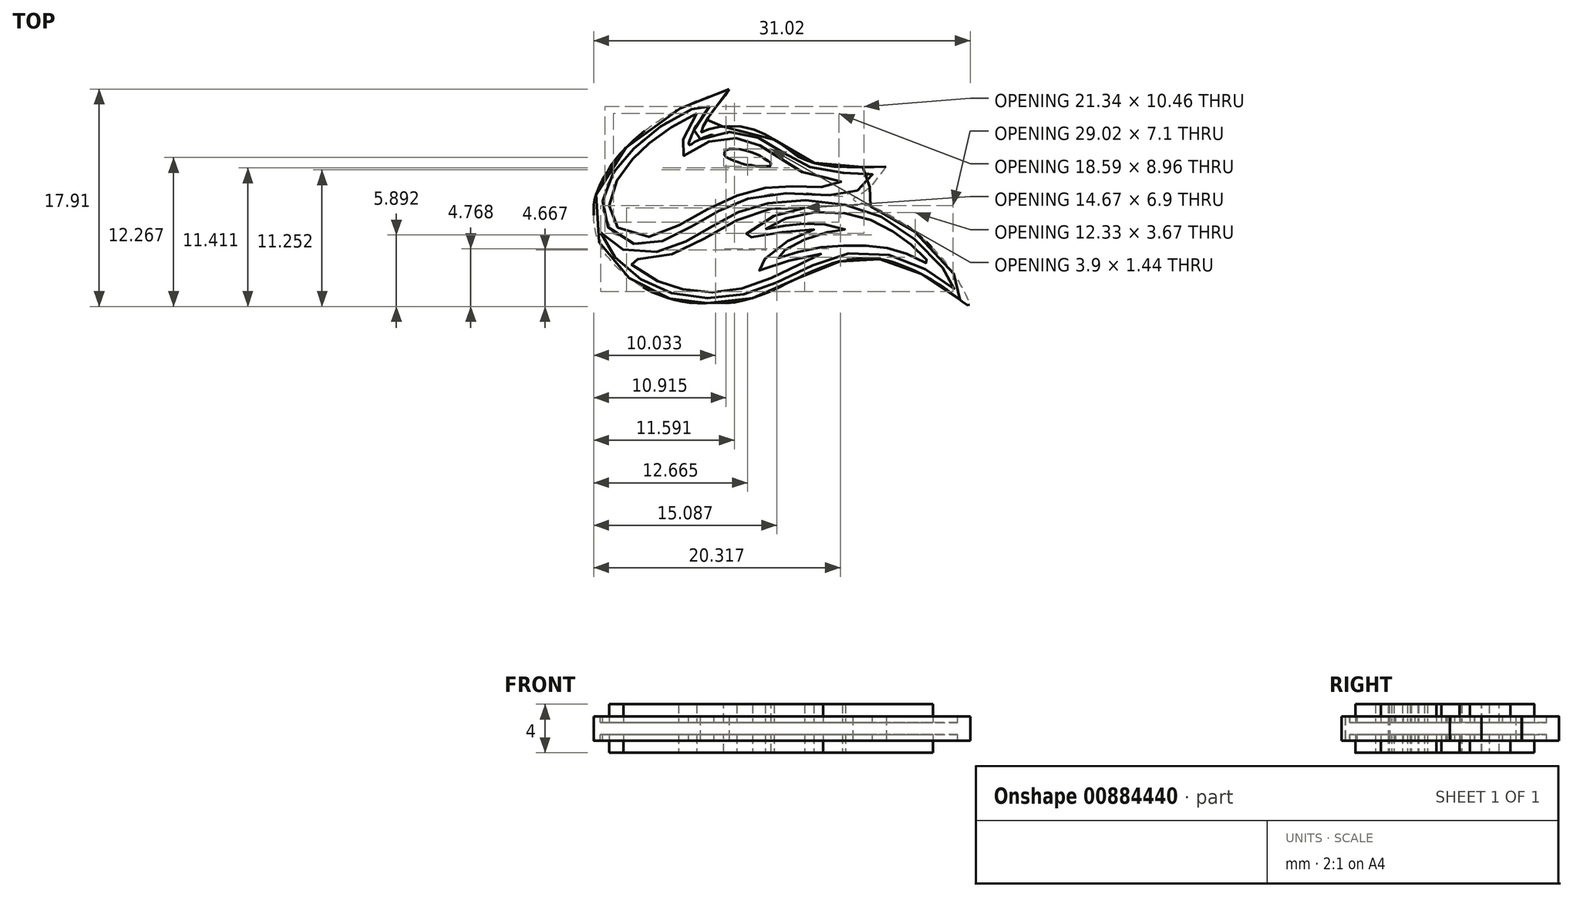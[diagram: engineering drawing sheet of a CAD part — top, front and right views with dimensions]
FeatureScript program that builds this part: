
annotation { "Feature Type Name" : "Feature", "Feature Type Description" : "" }
export const myFeature = defineFeature(function(context is Context, id is Id, definition is map)
    precondition{}
    {
        {
            var Q0;
            Q0=qCreatedBy(makeId("Top.planeOp"),FACE);
            var sketch = newSketch(context, id + "F0", { "sketchPlane" : qUnion([Q0])});
            skFitSpline(sketch, "E0", {"points": [v(-3.9, 9.38) * mm, v(-3.91, 9.32) * mm, v(-3.98, 9.21) * mm, v(-4.07, 9.09) * mm, v(-4.2, 8.93) * mm, v(-4.32, 8.78) * mm, v(-4.45, 8.61) * mm, v(-4.55, 8.47) * mm, v(-4.7, 8.28) * mm, v(-4.84, 8.11) * mm, v(-4.97, 7.93) * mm, v(-5.14, 7.74) * mm, v(-5.25, 7.58) * mm, v(-5.4, 7.4) * mm, v(-5.51, 7.23) * mm, v(-5.62, 7.08) * mm, v(-5.78, 6.83) * mm, v(-5.93, 6.6) * mm, v(-6, 6.44) * mm, v(-6.07, 6.28) * mm, v(-6.16, 6.11) * mm, v(-6.27, 5.97) * mm, v(-6.27, 5.87) * mm, v(-6.19, 5.85) * mm, v(-6.07, 5.91) * mm, v(-5.96, 5.94) * mm, v(-5.82, 6) * mm, v(-5.68, 6.05) * mm, v(-5.4, 6.13) * mm, v(-5.14, 6.2) * mm, v(-4.9, 6.26) * mm, v(-4.67, 6.3) * mm, v(-4.42, 6.32) * mm, v(-4.1, 6.34) * mm, v(-3.84, 6.34) * mm, v(-3.55, 6.33) * mm, v(-3.13, 6.33) * mm, v(-2.75, 6.3) * mm, v(-2.21, 6.16) * mm, v(-1.86, 6.04) * mm, v(-1.54, 5.92) * mm, v(-1.2, 5.78) * mm, v(-0.87, 5.63) * mm, v(-0.3, 5.3) * mm, v(0.1, 5.07) * mm, v(0.39, 4.86) * mm, v(0.8, 4.57) * mm, v(1.1, 4.33) * mm, v(1.5, 4.04) * mm, v(1.65, 3.9) * mm, v(1.9, 3.77) * mm, v(2, 3.7) * mm, v(2.22, 3.61) * mm, v(2.51, 3.51) * mm, v(2.63, 3.45) * mm, v(2.81, 3.42) * mm, v(3, 3.34) * mm, v(3.19, 3.28) * mm, v(3.49, 3.23) * mm, v(3.66, 3.16) * mm, v(3.9, 3.14) * mm, v(4.15, 3.12) * mm, v(4.42, 3.1) * mm, v(4.58, 3.04) * mm, v(4.9, 3) * mm, v(5.21, 3) * mm, v(5.71, 2.98) * mm, v(6.19, 2.98) * mm, v(6.67, 2.97) * mm, v(7.27, 2.98) * mm, v(7.68, 2.98) * mm, v(8.02, 2.98) * mm, v(8.43, 2.98) * mm, v(8.85, 3) * mm, v(9.02, 3) * mm, v(8.98, 2.92) * mm, v(8.74, 2.64) * mm, v(8.59, 2.42) * mm, v(8.3, 2.07) * mm, v(8.12, 1.82) * mm, v(7.95, 1.61) * mm, v(7.72, 1.36) * mm, v(7.51, 1.17) * mm, v(7.23, 0.94) * mm, v(7, 0.77) * mm, v(6.85, 0.64) * mm, v(6.63, 0.49) * mm, v(6.49, 0.42) * mm, v(6.37, 0.42) * mm, v(6.3, 0.38) * mm, v(6.29, 0.3) * mm, v(6.35, 0.25) * mm, v(6.47, 0.16) * mm, v(6.67, 0.12) * mm, v(6.88, 0.07) * mm, v(7.23, -0.05) * mm, v(7.57, -0.2) * mm, v(7.95, -0.34) * mm, v(8.36, -0.48) * mm, v(8.59, -0.6) * mm, v(8.98, -0.8) * mm, v(9.31, -0.98) * mm, v(9.63, -1.16) * mm, v(9.92, -1.34) * mm, v(10.16, -1.49) * mm, v(10.47, -1.68) * mm, v(10.78, -1.9) * mm, v(11.14, -2.17) * mm, v(11.43, -2.39) * mm, v(11.73, -2.62) * mm, v(12.02, -2.9) * mm, v(12.3, -3.12) * mm, v(12.66, -3.5) * mm, v(13, -3.84) * mm, v(13.23, -4.13) * mm, v(13.6, -4.5) * mm, v(13.87, -4.85) * mm, v(14.2, -5.31) * mm, v(14.55, -5.74) * mm, v(14.77, -6.1) * mm, v(15.02, -6.5) * mm, v(15.21, -6.85) * mm, v(15.4, -7.2) * mm, v(15.55, -7.47) * mm, v(15.7, -7.8) * mm, v(15.86, -8.15) * mm, v(15.92, -8.36) * mm, v(15.95, -8.5) * mm, v(15.74, -8.42) * mm, v(15.5, -8.22) * mm, v(15.25, -8.05) * mm, v(14.97, -7.83) * mm, v(14.64, -7.6) * mm, v(14.34, -7.38) * mm, v(14.17, -7.23) * mm, v(13.97, -7.09) * mm, v(13.68, -6.89) * mm, v(13.42, -6.72) * mm, v(13.16, -6.55) * mm, v(12.96, -6.42) * mm, v(12.72, -6.26) * mm, v(12.38, -6.07) * mm, v(12.15, -5.95) * mm, v(11.95, -5.85) * mm, v(11.7, -5.72) * mm, v(11.47, -5.6) * mm, v(11.22, -5.47) * mm, v(10.97, -5.37) * mm, v(10.74, -5.28) * mm, v(10.46, -5.18) * mm, v(10.16, -5.06) * mm, v(9.87, -4.94) * mm, v(9.64, -4.87) * mm, v(9.43, -4.79) * mm, v(9.16, -4.72) * mm, v(8.89, -4.65) * mm, v(8.63, -4.61) * mm, v(8.44, -4.6) * mm, v(8.2, -4.57) * mm, v(7.93, -4.54) * mm, v(7.58, -4.53) * mm, v(7.3, -4.54) * mm, v(7, -4.54) * mm, v(6.68, -4.54) * mm, v(6.49, -4.54) * mm, v(6.31, -4.58) * mm, v(6.15, -4.63) * mm, v(5.98, -4.66) * mm, v(5.74, -4.66) * mm, v(5.6, -4.69) * mm, v(5.44, -4.74) * mm, v(5.25, -4.77) * mm, v(5.09, -4.81) * mm, v(4.93, -4.86) * mm, v(4.83, -4.9) * mm, v(4.53, -4.97) * mm, v(4.2, -5.11) * mm, v(3.79, -5.26) * mm, v(3.54, -5.36) * mm, v(3.19, -5.5) * mm, v(2.96, -5.6) * mm, v(2.62, -5.77) * mm, v(2.36, -5.87) * mm, v(2.1, -6) * mm, v(1.88, -6.1) * mm, v(1.6, -6.24) * mm, v(1.36, -6.38) * mm, v(0.95, -6.56) * mm, v(0.58, -6.75) * mm, v(0.27, -6.9) * mm, v(-0.17, -7.08) * mm, v(-0.45, -7.23) * mm, v(-0.7, -7.35) * mm, v(-1.06, -7.49) * mm, v(-1.36, -7.59) * mm, v(-1.55, -7.66) * mm, v(-1.75, -7.74) * mm, v(-2.02, -7.82) * mm, v(-2.28, -7.9) * mm, v(-2.53, -7.97) * mm, v(-2.86, -8.05) * mm, v(-3.1, -8.13) * mm, v(-3.3, -8.16) * mm, v(-3.58, -8.2) * mm, v(-3.83, -8.21) * mm, v(-4.07, -8.22) * mm, v(-4.38, -8.22) * mm, v(-4.72, -8.2) * mm, v(-5.09, -8.2) * mm, v(-5.41, -8.2) * mm, v(-5.72, -8.22) * mm, v(-6.05, -8.21) * mm, v(-6.28, -8.23) * mm, v(-6.53, -8.22) * mm, v(-6.79, -8.23) * mm, v(-7, -8.21) * mm, v(-7.19, -8.2) * mm, v(-7.37, -8.16) * mm, v(-7.52, -8.15) * mm, v(-7.69, -8.11) * mm, v(-7.88, -8.1) * mm, v(-8.05, -8.06) * mm, v(-8.26, -8.02) * mm, v(-8.45, -7.96) * mm, v(-8.6, -7.91) * mm, v(-8.74, -7.88) * mm, v(-8.93, -7.81) * mm, v(-9.1, -7.76) * mm, v(-9.31, -7.7) * mm, v(-9.53, -7.6) * mm, v(-9.68, -7.55) * mm, v(-10.04, -7.42) * mm, v(-10.3, -7.3) * mm, v(-10.52, -7.19) * mm, v(-10.95, -6.96) * mm, v(-11.26, -6.77) * mm, v(-11.52, -6.6) * mm, v(-11.81, -6.4) * mm, v(-12.06, -6.23) * mm, v(-12.23, -6.08) * mm, v(-12.43, -5.93) * mm, v(-12.68, -5.72) * mm, v(-12.9, -5.53) * mm, v(-13.11, -5.32) * mm, v(-13.37, -5.05) * mm, v(-13.6, -4.76) * mm, v(-13.83, -4.5) * mm, v(-14.07, -4.23) * mm, v(-14.21, -3.97) * mm, v(-14.37, -3.74) * mm, v(-14.47, -3.5) * mm, v(-14.61, -3.23) * mm, v(-14.7, -3) * mm, v(-14.8, -2.77) * mm, v(-14.86, -2.53) * mm, v(-14.94, -2.3) * mm, v(-15, -1.83) * mm, v(-15.05, -1.58) * mm, v(-15.06, -1.24) * mm, v(-15.06, -0.85) * mm, v(-15.06, -0.53) * mm, v(-15.06, -0.3) * mm, v(-15, 0.2) * mm, v(-14.9, 0.6) * mm, v(-14.74, 1.08) * mm, v(-14.58, 1.42) * mm, v(-14.4, 1.83) * mm, v(-14.22, 2.15) * mm, v(-14.06, 2.42) * mm, v(-13.87, 2.7) * mm, v(-13.7, 3) * mm, v(-13.48, 3.3) * mm, v(-13.33, 3.51) * mm, v(-12.9, 4.05) * mm, v(-12.45, 4.52) * mm, v(-12.12, 4.83) * mm, v(-11.55, 5.38) * mm, v(-10.67, 6.1) * mm, v(-10.27, 6.4) * mm, v(-9.8, 6.73) * mm, v(-9.18, 7.11) * mm, v(-8.74, 7.38) * mm, v(-8.38, 7.58) * mm, v(-7.98, 7.79) * mm, v(-7.6, 8) * mm, v(-7.21, 8.15) * mm, v(-6.78, 8.36) * mm, v(-6.4, 8.5) * mm, v(-5.87, 8.72) * mm, v(-5.4, 8.9) * mm, v(-4.9, 9.08) * mm, v(-4.53, 9.2) * mm, v(-4.26, 9.3) * mm, v(-4.07, 9.37) * mm, v(-3.99, 9.4) * mm, v(-3.9, 9.38) * mm]});
            skFitSpline(sketch, "E1", {"points": [v(-5.52, 7.97) * mm, v(-5.3, 8.2) * mm, v(-5.17, 8.38) * mm, v(-5.51, 8.31) * mm, v(-5.76, 8.21) * mm, v(-6.27, 8.02) * mm, v(-6.63, 7.88) * mm, v(-6.9, 7.78) * mm, v(-7.32, 7.59) * mm, v(-7.78, 7.35) * mm, v(-8.2, 7.15) * mm, v(-8.66, 6.87) * mm, v(-9.12, 6.61) * mm, v(-9.46, 6.4) * mm, v(-9.72, 6.19) * mm, v(-10.04, 5.98) * mm, v(-10.31, 5.76) * mm, v(-10.75, 5.43) * mm, v(-11.11, 5.1) * mm, v(-11.47, 4.8) * mm, v(-11.86, 4.43) * mm, v(-12.13, 4.17) * mm, v(-12.41, 3.83) * mm, v(-12.7, 3.51) * mm, v(-12.94, 3.24) * mm, v(-13.17, 2.9) * mm, v(-13.4, 2.6) * mm, v(-13.45, 2.5) * mm, v(-13.63, 2.18) * mm, v(-13.8, 1.81) * mm, v(-14.02, 1.4) * mm, v(-14.1, 1.1) * mm, v(-14.24, 0.8) * mm, v(-14.28, 0.39) * mm, v(-14.34, 0.2) * mm, v(-14.32, 0) * mm, v(-14.34, -0.25) * mm, v(-14.32, -0.65) * mm, v(-14.3, -0.9) * mm, v(-14.24, -1.15) * mm, v(-14.16, -1.4) * mm, v(-14.03, -1.74) * mm, v(-13.87, -2) * mm, v(-13.63, -2.28) * mm, v(-13.43, -2.52) * mm, v(-13.05, -2.83) * mm, v(-12.58, -3.08) * mm, v(-12.27, -3.21) * mm, v(-12.03, -3.31) * mm, v(-11.75, -3.36) * mm, v(-11.5, -3.38) * mm, v(-11.25, -3.4) * mm, v(-10.9, -3.4) * mm, v(-10.57, -3.38) * mm, v(-10.28, -3.34) * mm, v(-9.92, -3.25) * mm, v(-9.55, -3.17) * mm, v(-9.32, -3.07) * mm, v(-9.07, -2.98) * mm, v(-8.78, -2.87) * mm, v(-8.43, -2.68) * mm, v(-8.08, -2.51) * mm, v(-7.62, -2.26) * mm, v(-7.08, -1.96) * mm, v(-6.73, -1.75) * mm, v(-6.35, -1.52) * mm, v(-6.07, -1.38) * mm, v(-5.75, -1.2) * mm, v(-5.4, -0.98) * mm, v(-5.1, -0.81) * mm, v(-4.84, -0.67) * mm, v(-4.49, -0.54) * mm, v(-4.18, -0.36) * mm, v(-3.9, -0.21) * mm, v(-3.57, -0.06) * mm, v(-3.17, 0.12) * mm, v(-2.79, 0.25) * mm, v(-2.4, 0.36) * mm, v(-1.86, 0.5) * mm, v(-1.32, 0.64) * mm, v(-0.8, 0.74) * mm, v(-0.26, 0.8) * mm, v(0.32, 0.83) * mm, v(1.01, 0.82) * mm, v(1.76, 0.84) * mm, v(2.44, 0.85) * mm, v(3.25, 0.82) * mm, v(3.97, 0.72) * mm, v(4.46, 0.63) * mm, v(4.92, 0.55) * mm, v(5.37, 0.55) * mm, v(5.74, 0.61) * mm, v(5.96, 0.7) * mm, v(6.28, 0.83) * mm, v(6.44, 0.91) * mm, v(6.6, 1.02) * mm, v(6.75, 1.13) * mm, v(6.91, 1.26) * mm, v(7.07, 1.38) * mm, v(7.23, 1.55) * mm, v(7.45, 1.76) * mm, v(7.58, 1.9) * mm, v(7.7, 2.05) * mm, v(7.79, 2.15) * mm, v(7.89, 2.26) * mm, v(7.9, 2.36) * mm, v(7.78, 2.47) * mm, v(7.63, 2.47) * mm, v(7.4, 2.47) * mm, v(7.1, 2.47) * mm, v(6.83, 2.46) * mm, v(6.4, 2.45) * mm, v(5.85, 2.48) * mm, v(5.38, 2.5) * mm, v(4.98, 2.53) * mm, v(4.49, 2.57) * mm, v(4.15, 2.65) * mm, v(3.64, 2.74) * mm, v(3.22, 2.82) * mm, v(2.83, 2.94) * mm, v(2.5, 3.04) * mm, v(2.2, 3.15) * mm, v(1.9, 3.27) * mm, v(1.55, 3.44) * mm, v(1.13, 3.74) * mm, v(0.89, 3.92) * mm, v(0.62, 4.1) * mm, v(0.4, 4.31) * mm, v(0.16, 4.46) * mm, v(-0.12, 4.64) * mm, v(-0.45, 4.84) * mm, v(-0.81, 5.04) * mm, v(-1.17, 5.25) * mm, v(-1.36, 5.33) * mm, v(-1.51, 5.4) * mm, v(-1.84, 5.52) * mm, v(-2.09, 5.62) * mm, v(-2.4, 5.7) * mm, v(-2.8, 5.76) * mm, v(-3.26, 5.79) * mm, v(-3.53, 5.85) * mm, v(-3.8, 5.87) * mm, v(-4.07, 5.87) * mm, v(-4.45, 5.84) * mm, v(-4.88, 5.76) * mm, v(-5.24, 5.66) * mm, v(-5.34, 5.63) * mm, v(-5.64, 5.53) * mm, v(-6.02, 5.39) * mm, v(-6.4, 5.23) * mm, v(-6.77, 5.04) * mm, v(-7.05, 4.83) * mm, v(-7.22, 4.79) * mm, v(-7.2, 5.08) * mm, v(-7.1, 5.36) * mm, v(-7, 5.59) * mm, v(-6.86, 5.93) * mm, v(-6.68, 6.27) * mm, v(-6.47, 6.6) * mm, v(-6.24, 6.9) * mm, v(-6.1, 7.16) * mm, v(-5.94, 7.42) * mm, v(-5.8, 7.59) * mm, v(-5.65, 7.75) * mm, v(-5.52, 7.97) * mm]});
            skFitSpline(sketch, "E2", {"points": [v(-14.5, -2.43) * mm, v(-14.32, -2.6) * mm, v(-14.14, -2.81) * mm, v(-13.88, -3.03) * mm, v(-13.76, -3.2) * mm, v(-13.49, -3.34) * mm, v(-13.28, -3.52) * mm, v(-12.98, -3.72) * mm, v(-12.65, -3.82) * mm, v(-12.34, -3.92) * mm, v(-12.05, -4.02) * mm, v(-11.75, -4.1) * mm, v(-11.17, -4.15) * mm, v(-10.73, -4.1) * mm, v(-10.16, -4.04) * mm, v(-9.74, -3.99) * mm, v(-9.4, -3.91) * mm, v(-9, -3.78) * mm, v(-8.67, -3.68) * mm, v(-8.36, -3.55) * mm, v(-8, -3.4) * mm, v(-7.71, -3.27) * mm, v(-7.42, -3.12) * mm, v(-6.99, -2.89) * mm, v(-6.7, -2.73) * mm, v(-6.34, -2.55) * mm, v(-6.16, -2.43) * mm, v(-5.94, -2.32) * mm, v(-5.7, -2.16) * mm, v(-5.45, -2.02) * mm, v(-5.13, -1.81) * mm, v(-4.84, -1.65) * mm, v(-4.54, -1.44) * mm, v(-4.25, -1.31) * mm, v(-3.95, -1.13) * mm, v(-3.72, -1.04) * mm, v(-3.47, -0.87) * mm, v(-3.15, -0.73) * mm, v(-2.88, -0.62) * mm, v(-2.57, -0.5) * mm, v(-2.24, -0.4) * mm, v(-1.92, -0.27) * mm, v(-1.57, -0.21) * mm, v(-1.4, -0.19) * mm, v(-1.06, -0.08) * mm, v(-0.34, 0.08) * mm, v(0, 0.1) * mm, v(0.2, 0.1) * mm, v(0.62, 0.14) * mm, v(1.2, 0.2) * mm, v(1.66, 0.22) * mm, v(2.52, 0.23) * mm, v(3.02, 0.17) * mm, v(3.45, 0.15) * mm, v(3.75, 0.12) * mm, v(4.3, 0.1) * mm, v(5.28, -0.08) * mm, v(5.8, -0.17) * mm, v(6.36, -0.29) * mm, v(6.83, -0.46) * mm, v(7.34, -0.62) * mm, v(7.87, -0.8) * mm, v(8.33, -1) * mm, v(8.87, -1.26) * mm, v(9.4, -1.58) * mm, v(9.89, -1.84) * mm, v(10.47, -2.25) * mm, v(10.87, -2.53) * mm, v(11.29, -2.89) * mm, v(11.75, -3.3) * mm, v(12.2, -3.67) * mm, v(12.56, -4.08) * mm, v(12.96, -4.52) * mm, v(13.4, -5.02) * mm, v(13.7, -5.34) * mm, v(13.9, -5.65) * mm, v(14.2, -6.08) * mm, v(14.52, -6.46) * mm, v(14.7, -6.74) * mm, v(14.85, -7.03) * mm, v(14.92, -7.21) * mm, v(14.66, -7.06) * mm, v(14.36, -6.81) * mm, v(14.1, -6.6) * mm, v(13.7, -6.32) * mm, v(13.37, -6.14) * mm, v(13.03, -5.9) * mm, v(12.49, -5.57) * mm, v(12.03, -5.32) * mm, v(11.46, -5.03) * mm, v(11.02, -4.84) * mm, v(10.64, -4.67) * mm, v(10.15, -4.51) * mm, v(9.58, -4.34) * mm, v(8.82, -4.17) * mm, v(8.22, -4.06) * mm, v(7.51, -4.03) * mm, v(6.8, -4.05) * mm, v(6.4, -4.07) * mm, v(5.89, -4.15) * mm, v(5.4, -4.27) * mm, v(4.92, -4.38) * mm, v(4.3, -4.58) * mm, v(3.84, -4.76) * mm, v(3.38, -4.95) * mm, v(2.93, -5.15) * mm, v(2.15, -5.54) * mm, v(1.58, -5.79) * mm, v(1.05, -6.04) * mm, v(0.63, -6.25) * mm, v(0.18, -6.44) * mm, v(-0.19, -6.61) * mm, v(-0.57, -6.77) * mm, v(-1.02, -6.93) * mm, v(-1.49, -7.13) * mm, v(-1.87, -7.25) * mm, v(-2.27, -7.36) * mm, v(-2.68, -7.5) * mm, v(-2.99, -7.56) * mm, v(-3.49, -7.67) * mm, v(-3.84, -7.78) * mm, v(-4.42, -7.8) * mm, v(-4.79, -7.83) * mm, v(-5.45, -7.82) * mm, v(-6, -7.82) * mm, v(-6.49, -7.81) * mm, v(-6.99, -7.74) * mm, v(-7.38, -7.68) * mm, v(-7.91, -7.6) * mm, v(-8.36, -7.5) * mm, v(-8.83, -7.35) * mm, v(-9.22, -7.21) * mm, v(-9.62, -7.04) * mm, v(-10, -6.92) * mm, v(-10.28, -6.78) * mm, v(-10.66, -6.58) * mm, v(-11.08, -6.35) * mm, v(-11.4, -6.12) * mm, v(-11.7, -5.93) * mm, v(-12.04, -5.7) * mm, v(-12.34, -5.42) * mm, v(-12.63, -5.16) * mm, v(-12.93, -4.87) * mm, v(-13.32, -4.45) * mm, v(-13.48, -4.23) * mm, v(-13.7, -3.9) * mm, v(-13.93, -3.57) * mm, v(-14.14, -3.26) * mm, v(-14.32, -2.99) * mm, v(-14.43, -2.77) * mm, v(-14.5, -2.57) * mm, v(-14.5, -2.43) * mm]});
            skFitSpline(sketch, "E3", {"points": [v(-6.57, 7.38) * mm, v(-6.74, 7.11) * mm, v(-6.9, 6.93) * mm, v(-7.03, 6.75) * mm, v(-7.13, 6.6) * mm, v(-7.22, 6.41) * mm, v(-7.3, 6.22) * mm, v(-7.38, 6.01) * mm, v(-7.47, 5.8) * mm, v(-7.59, 5.55) * mm, v(-7.66, 5.3) * mm, v(-7.75, 5.06) * mm, v(-7.8, 4.86) * mm, v(-7.85, 4.61) * mm, v(-7.92, 4.4) * mm, v(-7.97, 4.2) * mm, v(-8.02, 4.03) * mm, v(-8.04, 3.88) * mm, v(-8.07, 3.71) * mm, v(-8.03, 3.66) * mm, v(-7.9, 3.69) * mm, v(-7.82, 3.77) * mm, v(-7.65, 3.9) * mm, v(-7.47, 4.02) * mm, v(-7.27, 4.15) * mm, v(-7.13, 4.25) * mm, v(-6.98, 4.33) * mm, v(-6.8, 4.42) * mm, v(-6.61, 4.53) * mm, v(-6.44, 4.63) * mm, v(-6.22, 4.76) * mm, v(-5.92, 4.9) * mm, v(-5.67, 5.04) * mm, v(-5.42, 5.1) * mm, v(-5.18, 5.16) * mm, v(-4.96, 5.22) * mm, v(-4.74, 5.28) * mm, v(-4.52, 5.32) * mm, v(-4.3, 5.36) * mm, v(-4.14, 5.4) * mm, v(-3.97, 5.41) * mm, v(-3.78, 5.4) * mm, v(-3.57, 5.4) * mm, v(-3.35, 5.36) * mm, v(-3.14, 5.34) * mm, v(-3.01, 5.31) * mm, v(-2.84, 5.27) * mm, v(-2.66, 5.23) * mm, v(-2.45, 5.2) * mm, v(-2.3, 5.14) * mm, v(-2.13, 5.08) * mm, v(-1.97, 5.03) * mm, v(-1.81, 4.98) * mm, v(-1.67, 4.91) * mm, v(-1.54, 4.85) * mm, v(-1.38, 4.76) * mm, v(-1.18, 4.66) * mm, v(-0.98, 4.58) * mm, v(-0.85, 4.5) * mm, v(-0.69, 4.4) * mm, v(-0.55, 4.32) * mm, v(-0.4, 4.23) * mm, v(-0.22, 4.1) * mm, v(-0.08, 3.99) * mm, v(0.12, 3.85) * mm, v(0.24, 3.74) * mm, v(0.37, 3.65) * mm, v(0.51, 3.55) * mm, v(0.62, 3.46) * mm, v(0.73, 3.35) * mm, v(0.88, 3.24) * mm, v(1.04, 3.11) * mm, v(1.17, 3.03) * mm, v(1.33, 2.95) * mm, v(1.46, 2.89) * mm, v(1.58, 2.81) * mm, v(1.7, 2.76) * mm, v(1.88, 2.68) * mm, v(2.04, 2.62) * mm, v(2.16, 2.54) * mm, v(2.32, 2.49) * mm, v(2.5, 2.43) * mm, v(2.6, 2.4) * mm, v(2.72, 2.37) * mm, v(2.84, 2.33) * mm, v(3.02, 2.3) * mm, v(3.16, 2.24) * mm, v(3.3, 2.23) * mm, v(3.44, 2.22) * mm, v(3.6, 2.18) * mm, v(3.71, 2.16) * mm, v(3.89, 2.13) * mm, v(4.06, 2.1) * mm, v(4.26, 2.08) * mm, v(4.43, 2.08) * mm, v(4.55, 2.07) * mm, v(4.65, 2.06) * mm, v(4.77, 2.05) * mm, v(4.88, 2.04) * mm, v(5.02, 2.03) * mm, v(5.16, 2) * mm, v(5.3, 2) * mm, v(5.38, 1.99) * mm, v(5.4, 1.98) * mm, v(5.42, 1.93) * mm, v(5.4, 1.86) * mm, v(5.37, 1.82) * mm, v(5.31, 1.75) * mm, v(5.26, 1.68) * mm, v(5.22, 1.62) * mm, v(5.16, 1.58) * mm, v(5.1, 1.54) * mm, v(5.03, 1.46) * mm, v(4.97, 1.4) * mm, v(4.87, 1.34) * mm, v(4.75, 1.27) * mm, v(4.66, 1.22) * mm, v(4.52, 1.2) * mm, v(4.3, 1.21) * mm, v(4.09, 1.23) * mm, v(3.85, 1.29) * mm, v(3.57, 1.33) * mm, v(3.39, 1.33) * mm, v(3.12, 1.35) * mm, v(2.9, 1.36) * mm, v(2.7, 1.36) * mm, v(2.48, 1.37) * mm, v(2.26, 1.37) * mm, v(1.98, 1.38) * mm, v(1.7, 1.4) * mm, v(1.52, 1.4) * mm, v(1.31, 1.4) * mm, v(1.12, 1.39) * mm, v(0.86, 1.4) * mm, v(0.6, 1.4) * mm, v(0.36, 1.35) * mm, v(0.14, 1.35) * mm, v(-0.06, 1.35) * mm, v(-0.22, 1.33) * mm, v(-0.4, 1.3) * mm, v(-0.6, 1.3) * mm, v(-0.78, 1.28) * mm, v(-0.91, 1.26) * mm, v(-1.1, 1.23) * mm, v(-1.38, 1.18) * mm, v(-1.73, 1.1) * mm, v(-1.97, 1.02) * mm, v(-2.19, 0.97) * mm, v(-2.4, 0.91) * mm, v(-2.6, 0.86) * mm, v(-2.74, 0.8) * mm, v(-2.89, 0.76) * mm, v(-3.11, 0.66) * mm, v(-3.42, 0.56) * mm, v(-3.66, 0.48) * mm, v(-3.86, 0.4) * mm, v(-4.12, 0.29) * mm, v(-4.4, 0.15) * mm, v(-4.61, 0.05) * mm, v(-4.91, -0.07) * mm, v(-5.17, -0.2) * mm, v(-5.46, -0.37) * mm, v(-5.73, -0.5) * mm, v(-5.91, -0.6) * mm, v(-6.12, -0.73) * mm, v(-6.44, -0.9) * mm, v(-6.68, -1.05) * mm, v(-6.96, -1.23) * mm, v(-7.22, -1.36) * mm, v(-7.5, -1.53) * mm, v(-7.81, -1.7) * mm, v(-8.13, -1.88) * mm, v(-8.38, -2) * mm, v(-8.7, -2.16) * mm, v(-8.93, -2.28) * mm, v(-9.22, -2.41) * mm, v(-9.53, -2.5) * mm, v(-9.83, -2.64) * mm, v(-10.05, -2.72) * mm, v(-10.31, -2.77) * mm, v(-10.59, -2.77) * mm, v(-11.02, -2.84) * mm, v(-11.32, -2.83) * mm, v(-11.63, -2.78) * mm, v(-11.98, -2.67) * mm, v(-12.26, -2.58) * mm, v(-12.53, -2.44) * mm, v(-12.74, -2.33) * mm, v(-12.94, -2.13) * mm, v(-13.14, -1.94) * mm, v(-13.3, -1.78) * mm, v(-13.42, -1.62) * mm, v(-13.5, -1.5) * mm, v(-13.6, -1.32) * mm, v(-13.64, -1.2) * mm, v(-13.68, -1.06) * mm, v(-13.73, -0.92) * mm, v(-13.76, -0.8) * mm, v(-13.77, -0.63) * mm, v(-13.8, -0.5) * mm, v(-13.77, -0.31) * mm, v(-13.78, -0.19) * mm, v(-13.77, -0.06) * mm, v(-13.76, 0.07) * mm, v(-13.73, 0.18) * mm, v(-13.68, 0.39) * mm, v(-13.63, 0.68) * mm, v(-13.57, 0.88) * mm, v(-13.5, 1.09) * mm, v(-13.42, 1.33) * mm, v(-13.34, 1.51) * mm, v(-13.26, 1.68) * mm, v(-13.18, 1.82) * mm, v(-13.11, 1.96) * mm, v(-13.04, 2.1) * mm, v(-12.94, 2.24) * mm, v(-12.82, 2.44) * mm, v(-12.74, 2.53) * mm, v(-12.56, 2.75) * mm, v(-12.43, 2.96) * mm, v(-12.29, 3.1) * mm, v(-12.17, 3.3) * mm, v(-12.07, 3.43) * mm, v(-11.96, 3.54) * mm, v(-11.8, 3.68) * mm, v(-11.72, 3.77) * mm, v(-11.63, 3.86) * mm, v(-11.56, 3.94) * mm, v(-11.46, 4.04) * mm, v(-11.37, 4.18) * mm, v(-11.26, 4.3) * mm, v(-11.13, 4.4) * mm, v(-11.02, 4.49) * mm, v(-10.93, 4.57) * mm, v(-10.84, 4.65) * mm, v(-10.74, 4.72) * mm, v(-10.57, 4.86) * mm, v(-10.43, 4.99) * mm, v(-10.24, 5.13) * mm, v(-10.13, 5.24) * mm, v(-10.01, 5.33) * mm, v(-9.88, 5.44) * mm, v(-9.62, 5.6) * mm, v(-9.44, 5.72) * mm, v(-9.27, 5.83) * mm, v(-9.14, 5.95) * mm, v(-9, 6.05) * mm, v(-8.81, 6.17) * mm, v(-8.66, 6.26) * mm, v(-8.5, 6.35) * mm, v(-8.35, 6.44) * mm, v(-8.2, 6.55) * mm, v(-7.99, 6.7) * mm, v(-7.71, 6.84) * mm, v(-7.42, 7) * mm, v(-7.22, 7.13) * mm, v(-7, 7.23) * mm, v(-6.8, 7.31) * mm, v(-6.57, 7.38) * mm]});
            skFitSpline(sketch, "E4", {"points": [v(2.3, -0.4) * mm, v(2, -0.43) * mm, v(1.67, -0.48) * mm, v(1.25, -0.57) * mm, v(0.91, -0.67) * mm, v(0.56, -0.8) * mm, v(0.1, -0.93) * mm, v(-0.28, -1.09) * mm, v(-0.67, -1.27) * mm, v(-1, -1.47) * mm, v(-1.27, -1.65) * mm, v(-1.7, -1.91) * mm, v(-2.06, -2.17) * mm, v(-2.27, -2.37) * mm, v(-2.62, -2.57) * mm, v(-2.97, -2.79) * mm, v(-3.18, -2.93) * mm, v(-3.3, -3.05) * mm, v(-3.1, -3.06) * mm, v(-2.9, -3) * mm, v(-2.6, -2.93) * mm, v(-2.33, -2.88) * mm, v(-2.09, -2.81) * mm, v(-1.76, -2.77) * mm, v(-1.35, -2.69) * mm, v(-0.98, -2.63) * mm, v(-0.67, -2.57) * mm, v(-0.36, -2.52) * mm, v(0, -2.46) * mm, v(0.4, -2.4) * mm, v(0.91, -2.3) * mm, v(1.32, -2.23) * mm, v(1.74, -2.2) * mm, v(2.06, -2.2) * mm, v(2.5, -2.18) * mm, v(2.8, -2.17) * mm, v(3.07, -2.17) * mm, v(2.96, -2.26) * mm, v(2.75, -2.36) * mm, v(2.43, -2.45) * mm, v(2, -2.59) * mm, v(1.71, -2.72) * mm, v(1.42, -2.85) * mm, v(1.14, -3) * mm, v(0.81, -3.16) * mm, v(0.5, -3.33) * mm, v(0.28, -3.47) * mm, v(0.09, -3.61) * mm, v(-0.1, -3.75) * mm, v(-0.26, -3.94) * mm, v(-0.54, -4.17) * mm, v(-0.88, -4.5) * mm, v(-1.04, -4.69) * mm, v(-1.27, -4.97) * mm, v(-1.48, -5.12) * mm, v(-1.64, -5.26) * mm, v(-1.75, -5.45) * mm, v(-1.9, -5.61) * mm, v(-1.99, -5.71) * mm, v(-1.7, -5.64) * mm, v(-1.43, -5.54) * mm, v(-1.15, -5.46) * mm, v(-0.86, -5.35) * mm, v(-0.6, -5.28) * mm, v(-0.22, -5.15) * mm, v(0.14, -5.04) * mm, v(0.52, -4.91) * mm, v(0.89, -4.78) * mm, v(1.51, -4.62) * mm, v(2.02, -4.51) * mm, v(2.35, -4.41) * mm, v(2.72, -4.34) * mm, v(3.11, -4.26) * mm, v(3.45, -4.18) * mm, v(3.67, -4.17) * mm, v(3.83, -4.2) * mm, v(3.66, -4.29) * mm, v(3.45, -4.38) * mm, v(3.09, -4.52) * mm, v(2.8, -4.65) * mm, v(2.5, -4.8) * mm, v(2.1, -4.96) * mm, v(1.86, -5.07) * mm, v(1.57, -5.2) * mm, v(1.26, -5.35) * mm, v(0.85, -5.53) * mm, v(0.48, -5.72) * mm, v(0.1, -5.91) * mm, v(-0.18, -6.04) * mm, v(-0.46, -6.17) * mm, v(-0.8, -6.32) * mm, v(-1.08, -6.42) * mm, v(-1.53, -6.57) * mm, v(-1.89, -6.72) * mm, v(-2.21, -6.85) * mm, v(-2.52, -6.9) * mm, v(-2.84, -7.02) * mm, v(-3.2, -7.11) * mm, v(-3.64, -7.18) * mm, v(-3.94, -7.24) * mm, v(-4.23, -7.27) * mm, v(-4.53, -7.3) * mm, v(-4.77, -7.34) * mm, v(-5.13, -7.34) * mm, v(-5.43, -7.34) * mm, v(-5.8, -7.37) * mm, v(-6.06, -7.3) * mm, v(-6.49, -7.28) * mm, v(-7.03, -7.23) * mm, v(-7.2, -7.2) * mm, v(-7.47, -7.13) * mm, v(-7.7, -7.08) * mm, v(-7.96, -7.05) * mm, v(-8.28, -6.97) * mm, v(-8.45, -6.94) * mm, v(-8.7, -6.87) * mm, v(-8.94, -6.78) * mm, v(-9.18, -6.68) * mm, v(-9.47, -6.56) * mm, v(-9.68, -6.48) * mm, v(-9.98, -6.34) * mm, v(-10.32, -6.19) * mm, v(-10.62, -6) * mm, v(-10.93, -5.84) * mm, v(-11.24, -5.59) * mm, v(-11.49, -5.43) * mm, v(-11.76, -5.2) * mm, v(-12.05, -4.97) * mm, v(-12.27, -4.76) * mm, v(-12.49, -4.56) * mm, v(-12.6, -4.38) * mm, v(-12.36, -4.41) * mm, v(-12.12, -4.5) * mm, v(-12, -4.57) * mm, v(-11.73, -4.62) * mm, v(-11.45, -4.62) * mm, v(-11.09, -4.65) * mm, v(-10.6, -4.65) * mm, v(-10.1, -4.6) * mm, v(-9.74, -4.55) * mm, v(-9.3, -4.44) * mm, v(-8.79, -4.26) * mm, v(-8.28, -4.11) * mm, v(-7.91, -3.94) * mm, v(-7.51, -3.77) * mm, v(-7.1, -3.58) * mm, v(-6.74, -3.4) * mm, v(-6.3, -3.15) * mm, v(-5.71, -2.75) * mm, v(-5.2, -2.47) * mm, v(-4.77, -2.24) * mm, v(-4.3, -1.96) * mm, v(-3.88, -1.7) * mm, v(-3.46, -1.47) * mm, v(-3.02, -1.28) * mm, v(-2.65, -1.1) * mm, v(-2.24, -0.94) * mm, v(-1.67, -0.76) * mm, v(-1.24, -0.64) * mm, v(-0.78, -0.53) * mm, v(-0.14, -0.41) * mm, v(0.3, -0.39) * mm, v(0.73, -0.36) * mm, v(1.2, -0.29) * mm, v(1.59, -0.29) * mm, v(1.95, -0.29) * mm, v(2.3, -0.4) * mm]});
            skFitSpline(sketch, "E5", {"points": [v(-0.92, -2.12) * mm, v(-0.65, -2.07) * mm, v(-0.4, -1.98) * mm, v(-0.24, -1.96) * mm, v(0, -1.95) * mm, v(0.32, -1.89) * mm, v(0.64, -1.85) * mm, v(0.84, -1.8) * mm, v(1.11, -1.77) * mm, v(1.34, -1.74) * mm, v(1.55, -1.71) * mm, v(1.79, -1.7) * mm, v(2.02, -1.7) * mm, v(2.23, -1.69) * mm, v(2.5, -1.67) * mm, v(2.84, -1.67) * mm, v(3.13, -1.69) * mm, v(3.43, -1.7) * mm, v(3.68, -1.7) * mm, v(3.95, -1.74) * mm, v(4.33, -1.8) * mm, v(4.64, -1.83) * mm, v(4.99, -1.88) * mm, v(5.22, -1.97) * mm, v(5.43, -2) * mm, v(5.6, -2.14) * mm, v(5.69, -2.18) * mm, v(5.4, -2.23) * mm, v(5.17, -2.23) * mm, v(5.06, -2.25) * mm, v(4.83, -2.28) * mm, v(4.59, -2.35) * mm, v(4.18, -2.4) * mm, v(3.86, -2.5) * mm, v(3.51, -2.56) * mm, v(3.12, -2.7) * mm, v(2.76, -2.84) * mm, v(2.41, -2.97) * mm, v(2.04, -3.11) * mm, v(1.73, -3.3) * mm, v(1.49, -3.4) * mm, v(1.14, -3.59) * mm, v(0.9, -3.75) * mm, v(0.69, -3.86) * mm, v(0.43, -4.03) * mm, v(0.21, -4.18) * mm, v(0.05, -4.3) * mm, v(-0.13, -4.45) * mm, v(-0.2, -4.56) * mm, v(0, -4.55) * mm, v(0.13, -4.52) * mm, v(0.34, -4.43) * mm, v(0.58, -4.35) * mm, v(0.86, -4.25) * mm, v(1.2, -4.18) * mm, v(1.45, -4.1) * mm, v(1.74, -4.02) * mm, v(2.04, -3.95) * mm, v(2.35, -3.88) * mm, v(2.7, -3.77) * mm, v(3, -3.74) * mm, v(3.38, -3.67) * mm, v(3.78, -3.62) * mm, v(4.05, -3.6) * mm, v(4.45, -3.54) * mm, v(4.76, -3.52) * mm, v(5.07, -3.48) * mm, v(5.43, -3.5) * mm, v(5.7, -3.48) * mm, v(6.04, -3.48) * mm, v(6.38, -3.5) * mm, v(6.66, -3.5) * mm, v(7, -3.5) * mm, v(7.41, -3.5) * mm, v(7.77, -3.5) * mm, v(8.03, -3.5) * mm, v(8.24, -3.54) * mm, v(8.5, -3.58) * mm, v(8.82, -3.63) * mm, v(9.12, -3.7) * mm, v(9.36, -3.75) * mm, v(9.64, -3.81) * mm, v(9.86, -3.89) * mm, v(10.19, -3.98) * mm, v(10.44, -4.07) * mm, v(10.7, -4.16) * mm, v(10.98, -4.3) * mm, v(11.4, -4.45) * mm, v(11.64, -4.54) * mm, v(11.88, -4.66) * mm, v(12.1, -4.78) * mm, v(12.3, -4.92) * mm, v(12.5, -5.03) * mm, v(12.72, -5.17) * mm, v(12.9, -5.26) * mm, v(12.83, -5.12) * mm, v(12.75, -4.97) * mm, v(12.56, -4.82) * mm, v(12.33, -4.61) * mm, v(12.15, -4.43) * mm, v(11.9, -4.19) * mm, v(11.75, -4.03) * mm, v(11.49, -3.78) * mm, v(11.25, -3.55) * mm, v(11.05, -3.4) * mm, v(10.92, -3.28) * mm, v(10.66, -3.06) * mm, v(10.39, -2.86) * mm, v(10.05, -2.62) * mm, v(9.73, -2.43) * mm, v(9.43, -2.22) * mm, v(9.1, -2) * mm, v(8.8, -1.85) * mm, v(8.39, -1.62) * mm, v(8, -1.44) * mm, v(7.6, -1.32) * mm, v(7.21, -1.16) * mm, v(6.85, -1.07) * mm, v(6.43, -0.96) * mm, v(5.94, -0.86) * mm, v(5.16, -0.77) * mm, v(4.6, -0.72) * mm, v(4.06, -0.71) * mm, v(3.47, -0.7) * mm, v(2.94, -0.74) * mm, v(2.35, -0.85) * mm, v(1.77, -0.97) * mm, v(1.1, -1.14) * mm, v(0.79, -1.26) * mm, v(0.3, -1.42) * mm, v(0.28, -1.42) * mm, v(-0.12, -1.6) * mm, v(-0.57, -1.78) * mm, v(-0.8, -1.9) * mm, v(-0.92, -2.12) * mm]});
            skFitSpline(sketch, "E6", {"points": [v(-4.36, 4.06) * mm, v(-4.28, 3.9) * mm, v(-4.21, 3.82) * mm, v(-4.08, 3.73) * mm, v(-3.9, 3.66) * mm, v(-3.72, 3.58) * mm, v(-3.58, 3.52) * mm, v(-3.4, 3.44) * mm, v(-3.28, 3.4) * mm, v(-3.14, 3.36) * mm, v(-2.97, 3.31) * mm, v(-2.82, 3.26) * mm, v(-2.62, 3.22) * mm, v(-2.47, 3.18) * mm, v(-2.22, 3.16) * mm, v(-2, 3.1) * mm, v(-1.82, 3.07) * mm, v(-1.6, 3.04) * mm, v(-1.45, 3.04) * mm, v(-1.16, 3.04) * mm, v(-0.98, 3.03) * mm, v(-0.77, 3.03) * mm, v(-0.59, 3.02) * mm, v(-0.5, 3.08) * mm, v(-0.44, 3.2) * mm, v(-0.48, 3.32) * mm, v(-0.6, 3.39) * mm, v(-0.7, 3.49) * mm, v(-0.82, 3.55) * mm, v(-0.96, 3.64) * mm, v(-1.16, 3.74) * mm, v(-1.32, 3.9) * mm, v(-1.43, 3.95) * mm, v(-1.63, 4.04) * mm, v(-1.87, 4.16) * mm, v(-2.2, 4.23) * mm, v(-2.49, 4.3) * mm, v(-2.76, 4.4) * mm, v(-2.94, 4.43) * mm, v(-3.21, 4.45) * mm, v(-3.48, 4.47) * mm, v(-3.7, 4.47) * mm, v(-3.98, 4.45) * mm, v(-4.08, 4.41) * mm, v(-4.17, 4.33) * mm, v(-4.3, 4.23) * mm, v(-4.36, 4.06) * mm]});
            skSolve(sketch);
        }
        {
            var Q0;
            Q0=makeQuery(id+"F0.imprint","IMPRINT",FACE,{"disambiguationData":[TD([[makeQuery(id+"F0.imprint","IMPRINT",EDGE,{"derivedFrom":sQuery(id+"F0.wireOp",EDGE,"E0")}),-1.0]])]});
            extrude(context, id + "F1", {"entities" : qUnion([Q0]), "flatOperationType" : FlatOperationType.REMOVE, "depth" : 1 * mm, "offsetDistance" : 25.4 * mm, "hasSecondDirection" : true, "secondDirectionOppositeDirection" : true, "secondDirectionDepth" : 1 * mm, "domain" : OperationDomain.MODEL});
        }
        {
            var Q0;
            Q0=makeQuery(id+"F0.imprint","IMPRINT",FACE,{"disambiguationData":[TD([[makeQuery(id+"F0.imprint","IMPRINT",EDGE,{"derivedFrom":sQuery(id+"F0.wireOp",EDGE,"E1")}),1.0]])]});
            var Q1;
            Q1=makeQuery(id+"F0.imprint","IMPRINT",FACE,{"disambiguationData":[TD([[makeQuery(id+"F0.imprint","IMPRINT",EDGE,{"derivedFrom":sQuery(id+"F0.wireOp",EDGE,"E2")}),-1.0]])]});
            extrude(context, id + "F2", {"entities" : qUnion([Q0, Q1]), "operationType" : NewBodyOperationType.ADD, "depth" : .5 * mm, "offsetDistance" : 25.4 * mm, "hasSecondDirection" : true, "secondDirectionOppositeDirection" : true, "secondDirectionDepth" : .5 * mm});
        }
        {
            var Q0;
            Q0=makeQuery(id+"F0.imprint","IMPRINT",FACE,{"disambiguationData":[TD([[makeQuery(id+"F0.imprint","IMPRINT",EDGE,{"derivedFrom":sQuery(id+"F0.wireOp",EDGE,"E3")}),-1.0]])]});
            var Q1;
            Q1=makeQuery(id+"F0.imprint","IMPRINT",FACE,{"disambiguationData":[TD([[makeQuery(id+"F0.imprint","IMPRINT",EDGE,{"derivedFrom":sQuery(id+"F0.wireOp",EDGE,"E4")}),-1.0]])]});
            extrude(context, id + "F3", {"entities" : qUnion([Q0, Q1]), "operationType" : NewBodyOperationType.ADD, "depth" : 2 * mm, "offsetDistance" : 25.4 * mm, "hasSecondDirection" : true, "secondDirectionOppositeDirection" : true, "secondDirectionDepth" : 2 * mm});
        }
        {
            var Q0;
            Q0=makeQuery(id+"F0.imprint","IMPRINT",FACE,{"disambiguationData":[TD([[makeQuery(id+"F0.imprint","IMPRINT",EDGE,{"derivedFrom":sQuery(id+"F0.wireOp",EDGE,"E5")}),1.0]])]});
            extrude(context, id + "F4", {"entities" : qUnion([Q0]), "operationType" : NewBodyOperationType.ADD, "depth" : 2 * mm, "offsetDistance" : 25.4 * mm, "hasSecondDirection" : true, "secondDirectionOppositeDirection" : true, "secondDirectionDepth" : 2 * mm});
        }
        {
            var Q0;
            Q0=makeQuery(id+"F0.imprint","IMPRINT",FACE,{"disambiguationData":[TD([[makeQuery(id+"F0.imprint","IMPRINT",EDGE,{"derivedFrom":sQuery(id+"F0.wireOp",EDGE,"E6")}),1.0]])]});
            extrude(context, id + "F5", {"entities" : qUnion([Q0]), "operationType" : NewBodyOperationType.ADD, "depth" : .5 * mm, "offsetDistance" : 25.4 * mm, "hasSecondDirection" : true, "secondDirectionOppositeDirection" : true, "secondDirectionDepth" : .5 * mm});
        }
    });
